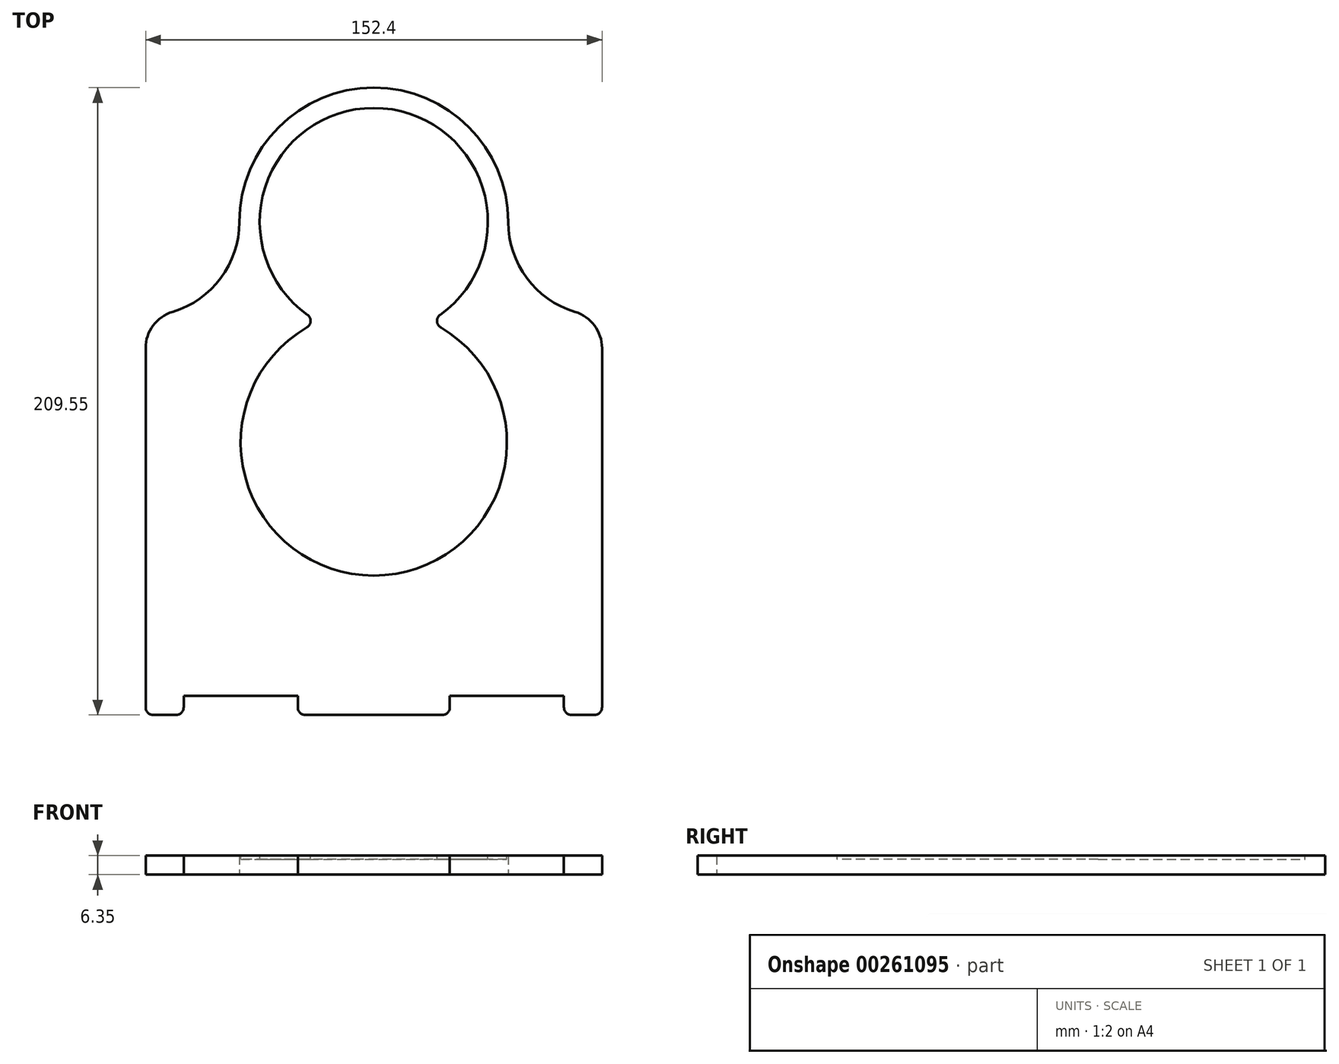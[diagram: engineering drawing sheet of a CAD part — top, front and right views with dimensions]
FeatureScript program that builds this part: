
annotation { "Feature Type Name" : "Feature", "Feature Type Description" : "" }
export const myFeature = defineFeature(function(context is Context, id is Id, definition is map)
    precondition{}
    {
        {
            var Q0;
            Q0=qCreatedBy(makeId("Top.planeOp"),FACE);
            var sketch = newSketch(context, id + "F0", { "sketchPlane" : qUnion([Q0])});
            skLineSegment(sketch, "E0.left", {"start": v(0, 0) * mm, "end": v(0, 127) * mm});
            skLineSegment(sketch, "E0.right", {"start": v(152.4, 0) * mm, "end": v(152.4, 127) * mm});
            skLineSegment(sketch, "E1.top", {"start": v(31.33, 158.33) * mm, "end": v(121.07, 158.33) * mm, "construction": true});
            skLineSegment(sketch, "E1.left", {"start": v(31.33, 127) * mm, "end": v(31.33, 158.33) * mm, "construction": true});
            skLineSegment(sketch, "E1.right", {"start": v(121.07, 127) * mm, "end": v(121.07, 158.33) * mm, "construction": true});
            skLineSegment(sketch, "E2", {"start": v(0, 127) * mm, "end": v(31.33, 127) * mm, "construction": true});
            skLineSegment(sketch, "E3", {"start": v(121.07, 127) * mm, "end": v(152.4, 127) * mm, "construction": true});
            skArc(sketch, "E4", {"start": v(0, 127) * mm, "mid": v(22.15, 136.18) * mm, "end": v(31.33, 158.33) * mm});
            skArc(sketch, "E5", {"start": v(121.07, 158.33) * mm, "mid": v(130.25, 136.18) * mm, "end": v(152.4, 127) * mm});
            skArc(sketch, "E6", {"start": v(121.07, 158.33) * mm, "mid": v(76.2, 203.2) * mm, "end": v(31.33, 158.33) * mm});
            skLineSegment(sketch, "E7", {"start": v(50.8, 0) * mm, "end": v(50.8, -6.35) * mm});
            skLineSegment(sketch, "E8", {"start": v(50.8, -6.35) * mm, "end": v(101.6, -6.35) * mm});
            skLineSegment(sketch, "E9", {"start": v(101.6, -6.35) * mm, "end": v(101.6, 0) * mm});
            skLineSegment(sketch, "E10", {"start": v(0, 0) * mm, "end": v(0, -6.35) * mm});
            skLineSegment(sketch, "E11", {"start": v(0, -6.35) * mm, "end": v(12.7, -6.35) * mm});
            skLineSegment(sketch, "E12", {"start": v(12.7, -6.35) * mm, "end": v(12.7, 0) * mm});
            skLineSegment(sketch, "E13", {"start": v(12.7, 0) * mm, "end": v(50.8, 0) * mm});
            skLineSegment(sketch, "E14", {"start": v(152.4, 0) * mm, "end": v(152.4, -6.35) * mm});
            skLineSegment(sketch, "E15", {"start": v(152.4, -6.35) * mm, "end": v(139.7, -6.35) * mm});
            skLineSegment(sketch, "E16", {"start": v(139.7, -6.35) * mm, "end": v(139.7, 0) * mm});
            skLineSegment(sketch, "E17", {"start": v(139.7, 0) * mm, "end": v(101.6, 0) * mm});
            skSolve(sketch);
        }
        {
            var Q0;
            Q0=makeQuery(id+"F0.imprint","IMPRINT",FACE,{"disambiguationData":[TD([[makeQuery(id+"F0.imprint","IMPRINT",EDGE,{"derivedFrom":sQuery(id+"F0.wireOp",EDGE,"E0.bottom")}),1.0]])]});
            var Q1;
            Q1=makeQuery(id+"F0.imprint","IMPRINT",FACE,{"disambiguationData":[TD([[makeQuery(id+"F0.imprint","IMPRINT",EDGE,{"derivedFrom":sQuery(id+"F0.wireOp",EDGE,"E0.left")}),-1.0]])]});
            extrude(context, id + "F1", {"entities" : qUnion([Q0, Q1]), "depth" : 6.35 * mm});
        }
        {
            var Q0;
            Q0=makeQuery(id+"F1.opExtrude","SWEPT_EDGE",EDGE,{"disambiguationData":[OSD([sQuery(id+"F0.wireOp",EDGE,"E0.left"),sQuery(id+"F0.wireOp",EDGE,"E4")])]});
            var Q1;
            Q1=makeQuery(id+"F1.opExtrude","SWEPT_EDGE",EDGE,{"disambiguationData":[OSD([sQuery(id+"F0.wireOp",EDGE,"E0.right"),sQuery(id+"F0.wireOp",EDGE,"E5")])]});
            fillet(context, id + "F2", {"entities" : qUnion([Q0, Q1]), "radius" : 12.7 * mm, "tangentPropagation" : true, "allowEdgeOverflow" : false});
        }
        {
            var Q0;
            Q0=makeQuery(id+"F1.opExtrude","SWEPT_EDGE",EDGE,{"disambiguationData":[OSD([sQuery(id+"F0.wireOp",EDGE,"E10"),sQuery(id+"F0.wireOp",EDGE,"E11")])]});
            var Q1;
            Q1=makeQuery(id+"F1.opExtrude","SWEPT_EDGE",EDGE,{"disambiguationData":[OSD([sQuery(id+"F0.wireOp",EDGE,"E11"),sQuery(id+"F0.wireOp",EDGE,"E12")])]});
            var Q2;
            Q2=makeQuery(id+"F1.opExtrude","SWEPT_EDGE",EDGE,{"disambiguationData":[OSD([sQuery(id+"F0.wireOp",EDGE,"E7"),sQuery(id+"F0.wireOp",EDGE,"E8")])]});
            var Q3;
            Q3=makeQuery(id+"F1.opExtrude","SWEPT_EDGE",EDGE,{"disambiguationData":[OSD([sQuery(id+"F0.wireOp",EDGE,"E8"),sQuery(id+"F0.wireOp",EDGE,"E9")])]});
            var Q4;
            Q4=makeQuery(id+"F1.opExtrude","SWEPT_EDGE",EDGE,{"disambiguationData":[OSD([sQuery(id+"F0.wireOp",EDGE,"E15"),sQuery(id+"F0.wireOp",EDGE,"E16")])]});
            var Q5;
            Q5=makeQuery(id+"F1.opExtrude","SWEPT_EDGE",EDGE,{"disambiguationData":[OSD([sQuery(id+"F0.wireOp",EDGE,"E14"),sQuery(id+"F0.wireOp",EDGE,"E15")])]});
            fillet(context, id + "F3", {"entities" : qUnion([Q0, Q1, Q2, Q3, Q4, Q5]), "radius" : 2.54 * mm, "tangentPropagation" : true, "allowEdgeOverflow" : false});
        }
        {
            var Q0;
            Q0=makeQuery(id+"F1.opExtrude","CAP_FACE",FACE,{"disambiguationData":[OSD([sQuery(id+"F0.wireOp",EDGE,"E0.left"),sQuery(id+"F0.wireOp",EDGE,"E0.right"),sQuery(id+"F0.wireOp",EDGE,"E4"),sQuery(id+"F0.wireOp",EDGE,"E5"),sQuery(id+"F0.wireOp",EDGE,"E6"),sQuery(id+"F0.wireOp",EDGE,"E7"),sQuery(id+"F0.wireOp",EDGE,"E8"),sQuery(id+"F0.wireOp",EDGE,"E9"),sQuery(id+"F0.wireOp",EDGE,"E10"),sQuery(id+"F0.wireOp",EDGE,"E11"),sQuery(id+"F0.wireOp",EDGE,"E12"),sQuery(id+"F0.wireOp",EDGE,"E13"),sQuery(id+"F0.wireOp",EDGE,"E14"),sQuery(id+"F0.wireOp",EDGE,"E15"),sQuery(id+"F0.wireOp",EDGE,"E16"),sQuery(id+"F0.wireOp",EDGE,"E17")])],"isStart":false});
            var sketch = newSketch(context, id + "F4", { "sketchPlane" : qUnion([Q0])});
            skCircle(sketch, "E18", {"center": v(76.2, 158.33) * mm, "radius": 38.1 * mm});
            skCircle(sketch, "E19", {"center": v(76.2, 84.66) * mm, "radius": 44.45 * mm});
            skLineSegment(sketch, "E20", {"start": v(76.2, 158.33) * mm, "end": v(76.2, -6.35) * mm, "construction": true});
            skSolve(sketch);
        }
        {
            var Q0;
            {var subQ0=sQuery(id+"F4.wireOp",EDGE,"E19");var subQ1=sQuery(id+"F4.wireOp",EDGE,"E18");var subQ2=makeQuery(id+"F4.imprint","INTERSECT",VERTEX,{"disambiguationData":[OD(0.0)],"derivedFrom":[subQ1,subQ0]});Q0=makeQuery(id+"F4.imprint","IMPRINT",FACE,{"disambiguationData":[TD([[makeQuery(id+"F4.imprint","IMPRINT",EDGE,{"disambiguationData":[TD([[subQ2,1.0]])],"derivedFrom":subQ1}),1.0]])]});}
            var Q1;
            {var subQ0=sQuery(id+"F4.wireOp",EDGE,"E19");var subQ1=sQuery(id+"F4.wireOp",EDGE,"E18");var subQ2=makeQuery(id+"F4.imprint","INTERSECT",VERTEX,{"disambiguationData":[OD(0.0)],"derivedFrom":[subQ1,subQ0]});Q1=makeQuery(id+"F4.imprint","IMPRINT",FACE,{"disambiguationData":[TD([[makeQuery(id+"F4.imprint","IMPRINT",EDGE,{"disambiguationData":[TD([[subQ2,-1.0]])],"derivedFrom":subQ1}),-1.0]])]});}
            var Q2;
            {var subQ0=sQuery(id+"F4.wireOp",EDGE,"E19");var subQ1=sQuery(id+"F4.wireOp",EDGE,"E18");var subQ2=makeQuery(id+"F4.imprint","INTERSECT",VERTEX,{"disambiguationData":[OD(0.0)],"derivedFrom":[subQ1,subQ0]});Q2=makeQuery(id+"F4.imprint","IMPRINT",FACE,{"disambiguationData":[TD([[makeQuery(id+"F4.imprint","IMPRINT",EDGE,{"disambiguationData":[TD([[subQ2,-1.0]])],"derivedFrom":subQ1}),1.0]])]});}
            var Q3;
            Q3=sQuery(id+"F4.wireOp",EDGE,"E20");
            var Q4;
            Q4=sQuery(id+"F4.wireOp",EDGE,"E19");
            var Q5;
            Q5=sQuery(id+"F4.wireOp",EDGE,"E18");
            extrude(context, id + "F5", {"entities" : qUnion([Q0, Q1, Q2]), "operationType" : NewBodyOperationType.REMOVE, "surfaceEntities" : qUnion([Q3, Q4, Q5]), "oppositeDirection" : true, "depth" : 1.27 * mm});
        }
        {
            var Q0;
            {var subQ0=sQuery(id+"F4.wireOp",EDGE,"E19");var subQ1=sQuery(id+"F4.wireOp",EDGE,"E18");Q0=makeQuery(id+"F5.boolean.opBoolean","COPY",EDGE,{"derivedFrom":makeQuery(id+"F5.opExtrude","SWEPT_EDGE",EDGE,{"disambiguationData":[OSD([subQ1,subQ0]),TDD([makeQuery(id+"F4.imprint","INTERSECT",VERTEX,{"disambiguationData":[OD(0.0)],"derivedFrom":[subQ1,subQ0]})])]})});}
            var Q1;
            {var subQ0=sQuery(id+"F4.wireOp",EDGE,"E19");var subQ1=sQuery(id+"F4.wireOp",EDGE,"E18");Q1=makeQuery(id+"F5.boolean.opBoolean","COPY",EDGE,{"derivedFrom":makeQuery(id+"F5.opExtrude","SWEPT_EDGE",EDGE,{"disambiguationData":[OSD([subQ1,subQ0]),TDD([makeQuery(id+"F4.imprint","INTERSECT",VERTEX,{"disambiguationData":[OD(1.0)],"derivedFrom":[subQ1,subQ0]})])]})});}
            fillet(context, id + "F6", {"entities" : qUnion([Q0, Q1]), "radius" : 2.54 * mm, "tangentPropagation" : true, "allowEdgeOverflow" : false});
        }
    });
